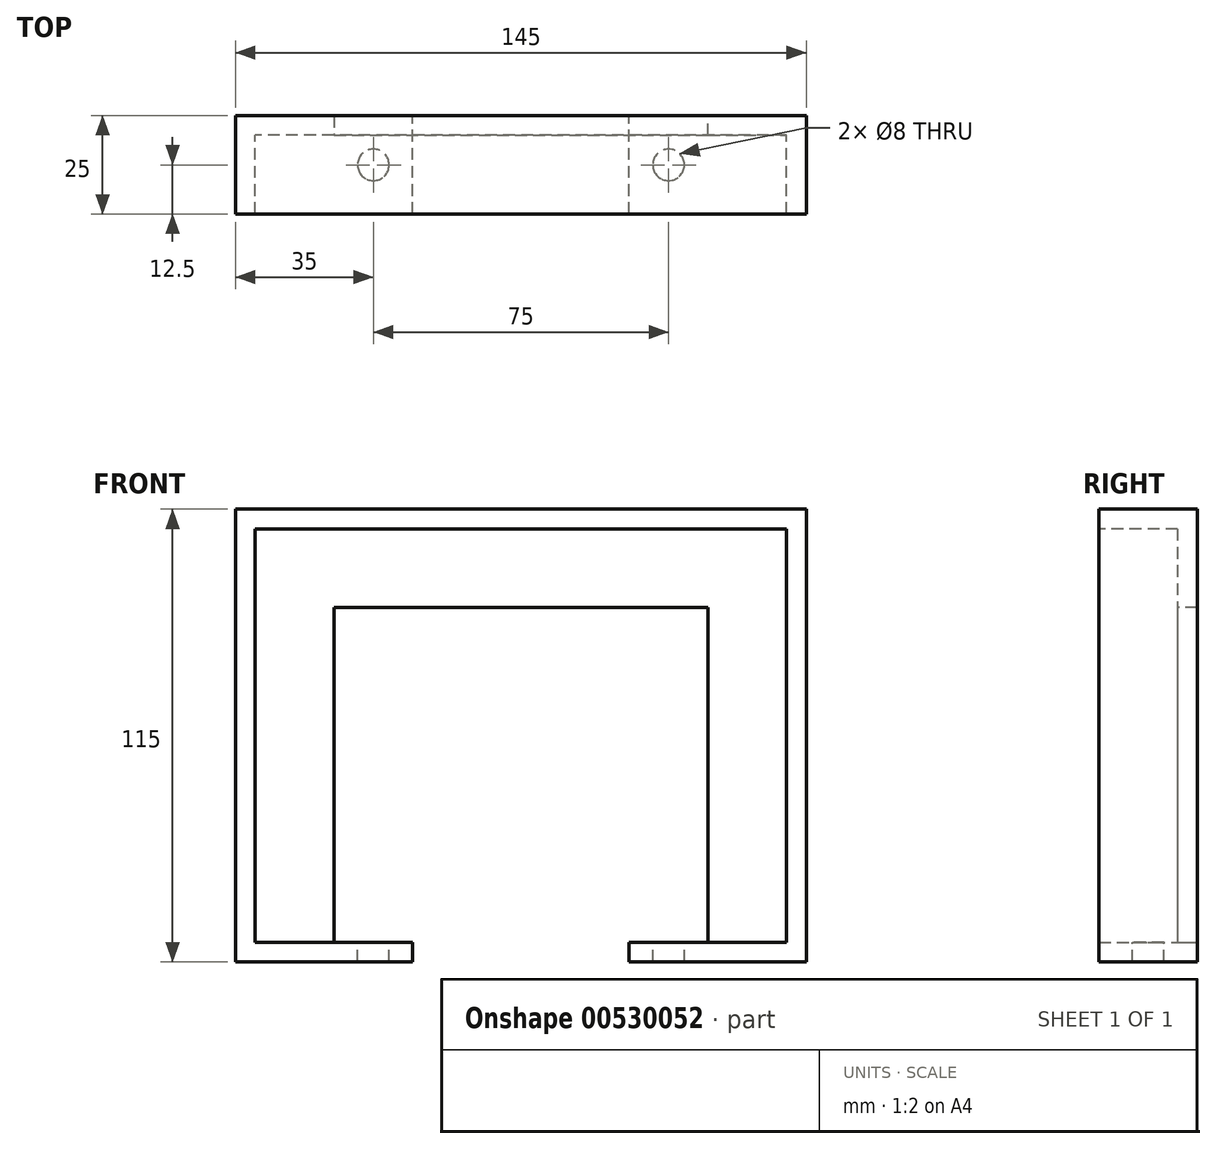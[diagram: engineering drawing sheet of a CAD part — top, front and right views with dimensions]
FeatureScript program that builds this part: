
annotation { "Feature Type Name" : "Feature", "Feature Type Description" : "" }
export const myFeature = defineFeature(function(context is Context, id is Id, definition is map)
    precondition{}
    {
        {
            var Q0;
            Q0=qCreatedBy(makeId("Right.planeOp"),FACE);
            var sketch = newSketch(context, id + "F0", { "sketchPlane" : qUnion([Q0])});
            skLineSegment(sketch, "E0.bottom", {"start": v(12.5, -57.5) * mm, "end": v(-12.5, -57.5) * mm});
            skLineSegment(sketch, "E0.top", {"start": v(12.5, 57.5) * mm, "end": v(-12.5, 57.5) * mm});
            skLineSegment(sketch, "E0.left", {"start": v(12.5, -57.5) * mm, "end": v(12.5, 57.5) * mm});
            skLineSegment(sketch, "E0.right", {"start": v(-12.5, -57.5) * mm, "end": v(-12.5, 57.5) * mm});
            skPoint(sketch, "E0.middle", {"position": v(0, 0) * mm});
            skSolve(sketch);
        }
        {
            var Q0;
            Q0=makeQuery(id+"F0.imprint","IMPRINT",FACE,{"disambiguationData":[TD([[makeQuery(id+"F0.imprint","IMPRINT",EDGE,{"derivedFrom":sQuery(id+"F0.wireOp",EDGE,"E0.bottom")}),-1.0]])]});
            extrude(context, id + "F1", {"entities" : qUnion([Q0]), "depth" : 5 * mm, "offsetDistance" : 25 * mm});
        }
        {
            var Q0;
            Q0=makeQuery(id+"F1.opExtrude","CAP_FACE",FACE,{"disambiguationData":[OSD([sQuery(id+"F0.wireOp",EDGE,"E0.bottom"),sQuery(id+"F0.wireOp",EDGE,"E0.top"),sQuery(id+"F0.wireOp",EDGE,"E0.left"),sQuery(id+"F0.wireOp",EDGE,"E0.right")])],"isStart":true});
            var sketch = newSketch(context, id + "F2", { "sketchPlane" : qUnion([Q0])});
            skLineSegment(sketch, "E1", {"start": v(-12.5, 57.5) * mm, "end": v(-12.5, 52.5) * mm});
            skLineSegment(sketch, "E2", {"start": v(-12.5, 52.5) * mm, "end": v(12.5, 52.5) * mm});
            skSolve(sketch);
        }
        {
            var Q0;
            Q0 = qSketchRegion(id + "F2", true);
            var Q1;
            Q1=makeQuery(id+"F2.imprint","IMPRINT",FACE,{"disambiguationData":[TD([[makeQuery(id+"F2.imprint","IMPRINT",EDGE,{"derivedFrom":sQuery(id+"F2.wireOp",EDGE,"E1")}),-1.0]])]});
            extrude(context, id + "F3", {"entities" : qUnion([Q0, Q1]), "operationType" : NewBodyOperationType.ADD, "depth" : 140 * mm, "offsetDistance" : 25 * mm});
        }
        {
            var Q0;
            Q0=makeQuery(id+"F3.opExtrude","SWEPT_FACE",FACE,{"disambiguationData":[OSD([sQuery(id+"F2.wireOp",EDGE,"E2")])]});
            var sketch = newSketch(context, id + "F4", { "sketchPlane" : qUnion([Q0])});
            skLineSegment(sketch, "E3", {"start": v(-140, 12.5) * mm, "end": v(-135, 12.5) * mm});
            skLineSegment(sketch, "E4", {"start": v(-135, 12.5) * mm, "end": v(-135, -12.5) * mm});
            skSolve(sketch);
        }
        {
            var Q0;
            Q0=makeQuery(id+"F4.imprint","IMPRINT",FACE,{"disambiguationData":[TD([[makeQuery(id+"F4.imprint","IMPRINT",EDGE,{"derivedFrom":sQuery(id+"F4.wireOp",EDGE,"E3")}),-1.0]])]});
            extrude(context, id + "F5", {"entities" : qUnion([Q0]), "operationType" : NewBodyOperationType.ADD, "depth" : 110 * mm, "offsetDistance" : 25 * mm});
        }
        {
            var Q0;
            Q0=makeQuery(id+"F5.opExtrude","SWEPT_FACE",FACE,{"disambiguationData":[OSD([sQuery(id+"F4.wireOp",EDGE,"E4")])]});
            var sketch = newSketch(context, id + "F6", { "sketchPlane" : qUnion([Q0])});
            skLineSegment(sketch, "E5", {"start": v(-12.5, -57.5) * mm, "end": v(-12.5, -52.5) * mm});
            skLineSegment(sketch, "E6", {"start": v(-12.5, -52.5) * mm, "end": v(12.5, -52.5) * mm});
            skSolve(sketch);
        }
        {
            var Q0;
            Q0 = qSketchRegion(id + "F6", true);
            var Q1;
            Q1=makeQuery(id+"F6.imprint","IMPRINT",FACE,{"disambiguationData":[TD([[makeQuery(id+"F6.imprint","IMPRINT",EDGE,{"derivedFrom":sQuery(id+"F6.wireOp",EDGE,"E5")}),-1.0]])]});
            extrude(context, id + "F7", {"entities" : qUnion([Q0, Q1]), "operationType" : NewBodyOperationType.ADD, "depth" : 40 * mm, "offsetDistance" : 25 * mm});
        }
        {
            var Q0;
            Q0=makeQuery(id+"F1.opExtrude","CAP_FACE",FACE,{"disambiguationData":[OSD([sQuery(id+"F0.wireOp",EDGE,"E0.bottom"),sQuery(id+"F0.wireOp",EDGE,"E0.top"),sQuery(id+"F0.wireOp",EDGE,"E0.left"),sQuery(id+"F0.wireOp",EDGE,"E0.right")])],"isStart":true});
            var sketch = newSketch(context, id + "F8", { "sketchPlane" : qUnion([Q0])});
            skLineSegment(sketch, "E7", {"start": v(12.5, -57.5) * mm, "end": v(12.5, -52.5) * mm});
            skLineSegment(sketch, "E8", {"start": v(12.5, -52.5) * mm, "end": v(-12.5, -52.5) * mm});
            skSolve(sketch);
        }
        {
            var Q0;
            Q0 = qSketchRegion(id + "F8", true);
            var Q1;
            Q1=makeQuery(id+"F8.imprint","IMPRINT",FACE,{"disambiguationData":[TD([[makeQuery(id+"F8.imprint","IMPRINT",EDGE,{"derivedFrom":sQuery(id+"F8.wireOp",EDGE,"E7")}),1.0]])]});
            extrude(context, id + "F9", {"entities" : qUnion([Q0, Q1]), "operationType" : NewBodyOperationType.ADD, "depth" : 40 * mm, "offsetDistance" : 25 * mm});
        }
        {
            var Q0;
            Q0=makeQuery(id+"F5.opExtrude","SWEPT_FACE",FACE,{"disambiguationData":[OSD([sQuery(id+"F4.wireOp",EDGE,"E4")])]});
            var sketch = newSketch(context, id + "F10", { "sketchPlane" : qUnion([Q0])});
            skLineSegment(sketch, "E9", {"start": v(12.5, 52.5) * mm, "end": v(7.5, 52.5) * mm});
            skLineSegment(sketch, "E10", {"start": v(7.5, 52.5) * mm, "end": v(7.5, -52.5) * mm});
            skSolve(sketch);
        }
        {
            var Q0;
            Q0=makeQuery(id+"F10.imprint","IMPRINT",FACE,{"disambiguationData":[TD([[makeQuery(id+"F10.imprint","IMPRINT",EDGE,{"derivedFrom":sQuery(id+"F10.wireOp",EDGE,"E9")}),-1.0]])]});
            extrude(context, id + "F11", {"entities" : qUnion([Q0]), "operationType" : NewBodyOperationType.ADD, "depth" : 20 * mm, "offsetDistance" : 25 * mm});
        }
        {
            var Q0;
            Q0=makeQuery(id+"F1.opExtrude","CAP_FACE",FACE,{"disambiguationData":[OSD([sQuery(id+"F0.wireOp",EDGE,"E0.bottom"),sQuery(id+"F0.wireOp",EDGE,"E0.top"),sQuery(id+"F0.wireOp",EDGE,"E0.left"),sQuery(id+"F0.wireOp",EDGE,"E0.right")])],"isStart":true});
            var sketch = newSketch(context, id + "F12", { "sketchPlane" : qUnion([Q0])});
            skLineSegment(sketch, "E11", {"start": v(-12.5, 52.5) * mm, "end": v(-7.5, 52.5) * mm});
            skLineSegment(sketch, "E12", {"start": v(-7.5, 52.5) * mm, "end": v(-7.5, -52.5) * mm});
            skSolve(sketch);
        }
        {
            var Q0;
            Q0=makeQuery(id+"F12.imprint","IMPRINT",FACE,{"disambiguationData":[TD([[makeQuery(id+"F12.imprint","IMPRINT",EDGE,{"derivedFrom":sQuery(id+"F12.wireOp",EDGE,"E11")}),-1.0]])]});
            extrude(context, id + "F13", {"entities" : qUnion([Q0]), "operationType" : NewBodyOperationType.ADD, "depth" : 20 * mm, "offsetDistance" : 25 * mm});
        }
        {
            var Q0;
            Q0=makeQuery(id+"F13.opExtrude","CAP_FACE",FACE,{"disambiguationData":[OSD([sQuery(id+"F0.wireOp",EDGE,"E0.left"),sQuery(id+"F8.wireOp",EDGE,"E8"),sQuery(id+"F12.wireOp",EDGE,"E11"),sQuery(id+"F12.wireOp",EDGE,"E12")])],"isStart":false});
            var sketch = newSketch(context, id + "F14", { "sketchPlane" : qUnion([Q0])});
            skLineSegment(sketch, "E13", {"start": v(-12.5, 52.5) * mm, "end": v(-12.5, 32.5) * mm});
            skLineSegment(sketch, "E14", {"start": v(-12.5, 32.5) * mm, "end": v(-7.5, 32.5) * mm});
            skSolve(sketch);
        }
        {
            var Q0;
            Q0 = qSketchRegion(id + "F14", true);
            var Q1;
            Q1=makeQuery(id+"F14.imprint","IMPRINT",FACE,{"disambiguationData":[TD([[makeQuery(id+"F14.imprint","IMPRINT",EDGE,{"derivedFrom":sQuery(id+"F14.wireOp",EDGE,"E13")}),-1.0]])]});
            extrude(context, id + "F15", {"entities" : qUnion([Q0, Q1]), "operationType" : NewBodyOperationType.ADD, "depth" : 97.6 * mm, "offsetDistance" : 25 * mm});
        }
        {
            var Q0;
            {var subQ0=sQuery(id+"F0.wireOp",EDGE,"E0.right");Q0=makeQuery(id+"F9.boolean.opBoolean","MERGE",FACE,{"derivedFrom":[makeQuery(id+"F7.boolean.opBoolean","MERGE",FACE,{"derivedFrom":[makeQuery(id+"F5.boolean.opBoolean","MERGE",FACE,{"derivedFrom":[makeQuery(id+"F3.boolean.opBoolean","MERGE",FACE,{"derivedFrom":[makeQuery(id+"F1.opExtrude","SWEPT_FACE",FACE,{"disambiguationData":[OSD([subQ0])]}),makeQuery(id+"F3.opExtrude","SWEPT_FACE",FACE,{"disambiguationData":[OSD([subQ0])]})]}),makeQuery(id+"F5.opExtrude","SWEPT_FACE",FACE,{"disambiguationData":[OSD([sQuery(id+"F4.wireOp",EDGE,"E3")])]})]}),makeQuery(id+"F7.opExtrude","SWEPT_FACE",FACE,{"disambiguationData":[OSD([sQuery(id+"F6.wireOp",EDGE,"E5")])]})]}),makeQuery(id+"F9.opExtrude","SWEPT_FACE",FACE,{"disambiguationData":[OSD([sQuery(id+"F8.wireOp",EDGE,"E7")])]})]});}
            var sketch = newSketch(context, id + "F16", { "sketchPlane" : qUnion([Q0])});
            skLineSegment(sketch, "E15", {"start": v(-135, -52.5) * mm, "end": v(-140, -52.5) * mm});
            skLineSegment(sketch, "E16", {"start": v(0, -52.5) * mm, "end": v(5, -52.5) * mm});
            skSolve(sketch);
        }
        {
            var Q0;
            {var subQ0=sQuery(id+"F6.wireOp",EDGE,"E6");Q0=makeQuery(id+"F7K4NsKEcpMP7Oz_1.boolean.opBoolean","MERGE",FACE,{"derivedFrom":[makeQuery(id+"F7.opExtrude","SWEPT_FACE",FACE,{"disambiguationData":[OSD([subQ0])]}),makeQuery(id+"F7K4NsKEcpMP7Oz_1.opExtrude","SWEPT_FACE",FACE,{"disambiguationData":[OSD([sQuery(id+"F0.wireOp",EDGE,"E0.right"),sQuery(id+"F2.wireOp",EDGE,"E2"),sQuery(id+"F4.wireOp",EDGE,"E3"),sQuery(id+"F4.wireOp",EDGE,"E4"),sQuery(id+"F6.wireOp",EDGE,"E5"),subQ0,sQuery(id+"F16.wireOp",EDGE,"E15")])]})]});}
            var sketch = newSketch(context, id + "F17", { "sketchPlane" : qUnion([Q0])});
            skCircle(sketch, "E17", {"center": v(-105, 0) * mm, "radius": 4 * mm});
            skSolve(sketch);
        }
        {
            var Q0;
            Q0=makeQuery(id+"F17.imprint","IMPRINT",FACE,{"disambiguationData":[TD([[makeQuery(id+"F17.imprint","IMPRINT",EDGE,{"derivedFrom":sQuery(id+"F17.wireOp",EDGE,"E17")}),1.0]])]});
            extrude(context, id + "F18", {"entities" : qUnion([Q0]), "operationType" : NewBodyOperationType.REMOVE, "oppositeDirection" : true, "depth" : 25 * mm, "offsetDistance" : 25 * mm});
        }
        {
            var Q0;
            {var subQ0=sQuery(id+"F8.wireOp",EDGE,"E8");Q0=makeQuery(id+"F7K4NsKEcpMP7Oz_1.boolean.opBoolean","MERGE",FACE,{"derivedFrom":[makeQuery(id+"F9.opExtrude","SWEPT_FACE",FACE,{"disambiguationData":[OSD([subQ0])]}),makeQuery(id+"F7K4NsKEcpMP7Oz_1.opExtrude","SWEPT_FACE",FACE,{"disambiguationData":[OSD([sQuery(id+"F0.wireOp",EDGE,"E0.right"),sQuery(id+"F8.wireOp",EDGE,"E7"),subQ0,sQuery(id+"F16.wireOp",EDGE,"E16")])]})]});}
            var sketch = newSketch(context, id + "F19", { "sketchPlane" : qUnion([Q0])});
            skCircle(sketch, "E18", {"center": v(-30, 0) * mm, "radius": 4 * mm});
            skSolve(sketch);
        }
        {
            var Q0;
            Q0 = qSketchRegion(id + "F19", true);
            extrude(context, id + "F20", {"entities" : qUnion([Q0]), "operationType" : NewBodyOperationType.REMOVE, "oppositeDirection" : true, "depth" : 15 * mm, "offsetDistance" : 25 * mm});
        }
        {
            var Q0;
            Q0 = qSketchRegion(id + "F17", true);
            extrude(context, id + "F21", {"entities" : qUnion([Q0]), "operationType" : NewBodyOperationType.REMOVE, "oppositeDirection" : true, "depth" : 25 * mm, "offsetDistance" : 25 * mm});
        }
        {
            var Q0;
            Q0 = qSketchRegion(id + "F19", true);
            extrude(context, id + "F22", {"entities" : qUnion([Q0]), "operationType" : NewBodyOperationType.REMOVE, "oppositeDirection" : true, "depth" : 25 * mm, "offsetDistance" : 25 * mm});
        }
    });
